# Revit family: Bath-Freestanding-Caroma Cube 1600a
name_source: partatom
category: Plumbing Fixtures
revit_build: Autodesk Revit 2014 (Build: 20131024_2115(x64)
units: mm (PartAtom-declared; Revit-internal decimal feet)

## types (1)
- Standard
    Assembly Code = C1030210
    CW Connection = No
    Capacity_ANZRS = 375.0 L
    Cost = 1599 $
    Default Elevation = 0 mm  [stored 0 ft]
    Description = Caroma Cube 1600 Freestanding Bath
    HW Connection = No
    Height_ANZRS = 560 mm  [stored 1.83727 ft]
    Keynote = BT
    Length_ANZRS = 1600 mm  [stored 5.24934 ft]
    Manufacturer = GWA Bathrooms & Kitchens
    Material_ANZRS = Porcelain-White-Caroma
    Model = CU6W
    ModifiedIssue_ANZRS = 20141003.01 $
    PlumbingMaterial_ANZRS = PVC-White-Caroma
    Type Comments = Integrated adjustable feet included, Footlocker fittings included, no overflow, plug & waste not included, white only
    URL = http://www.caroma.com.au
    Vent Connection = No
    WFU = 4
    Waste = Metal-Chrome-Caroma
    Waste Connection = Yes
    Width_ANZRS = 768 mm  [stored 2.51969 ft]

note: [stored X ft] marks values corroborated as IEEE doubles in the binary element streams (Revit-internal decimal feet)

## geometry (parser evidence)
native form markers: Blend x12, Sweep x1
no freeform markers — native parametric forms only
